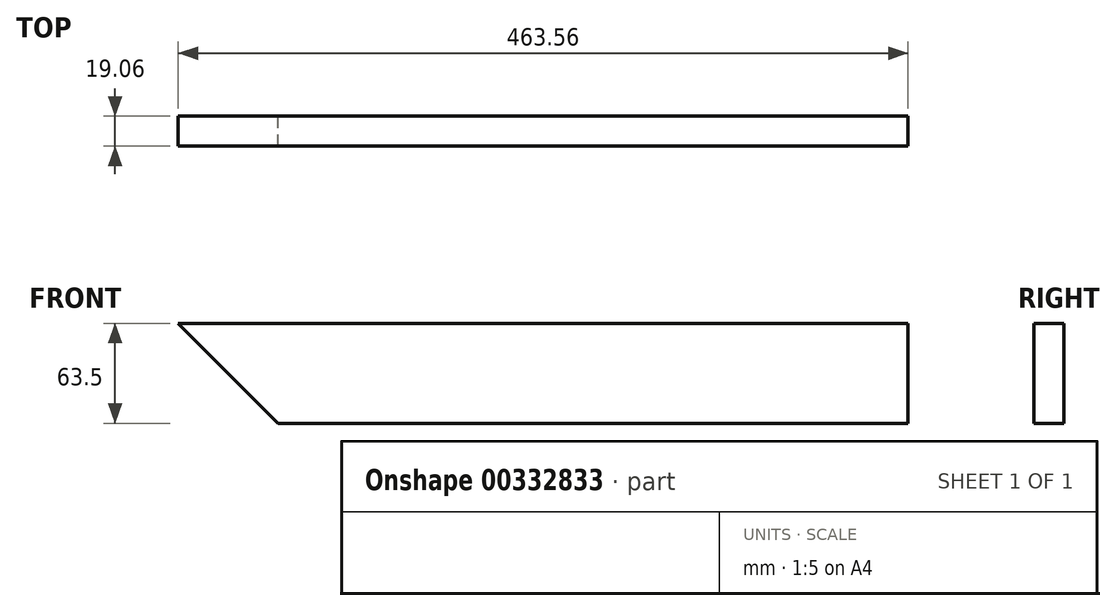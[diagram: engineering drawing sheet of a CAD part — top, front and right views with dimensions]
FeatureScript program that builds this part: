
annotation { "Feature Type Name" : "Feature", "Feature Type Description" : "" }
export const myFeature = defineFeature(function(context is Context, id is Id, definition is map)
    precondition{}
    {
        {
            var Q0;
            Q0=qCreatedBy(makeId("Front.planeOp"),FACE);
            var sketch = newSketch(context, id + "F0", { "sketchPlane" : qUnion([Q0])});
            skLineSegment(sketch, "E0.bottom", {"start": v(231.78, 31.75) * mm, "end": v(-231.78, 31.75) * mm});
            skLineSegment(sketch, "E0.top", {"start": v(231.78, -31.75) * mm, "end": v(-168.27, -31.75) * mm});
            skLineSegment(sketch, "E0.left", {"start": v(231.77, 31.75) * mm, "end": v(231.77, -31.75) * mm});
            skPoint(sketch, "E0.middle", {"position": v(0, 0) * mm});
            skPoint(sketch, "E0.right.start.orphan", {"position": v(-231.78, 31.75) * mm});
            skLineSegment(sketch, "E1", {"start": v(-231.77, 31.75) * mm, "end": v(-168.27, -31.75) * mm});
            skPoint(sketch, "E2.orphan", {"position": v(-231.78, -31.75) * mm});
            skSolve(sketch);
        }
        {
            var Q0;
            Q0=makeQuery(id+"F0.imprint","IMPRINT",FACE,{"disambiguationData":[TD([[makeQuery(id+"F0.imprint","IMPRINT",EDGE,{"derivedFrom":sQuery(id+"F0.wireOp",EDGE,"E0.bottom")}),1.0]])]});
            extrude(context, id + "F1", {"entities" : qUnion([Q0]), "endBound" : BoundingType.SYMMETRIC, "depth" : 19.05 * mm});
        }
    });
